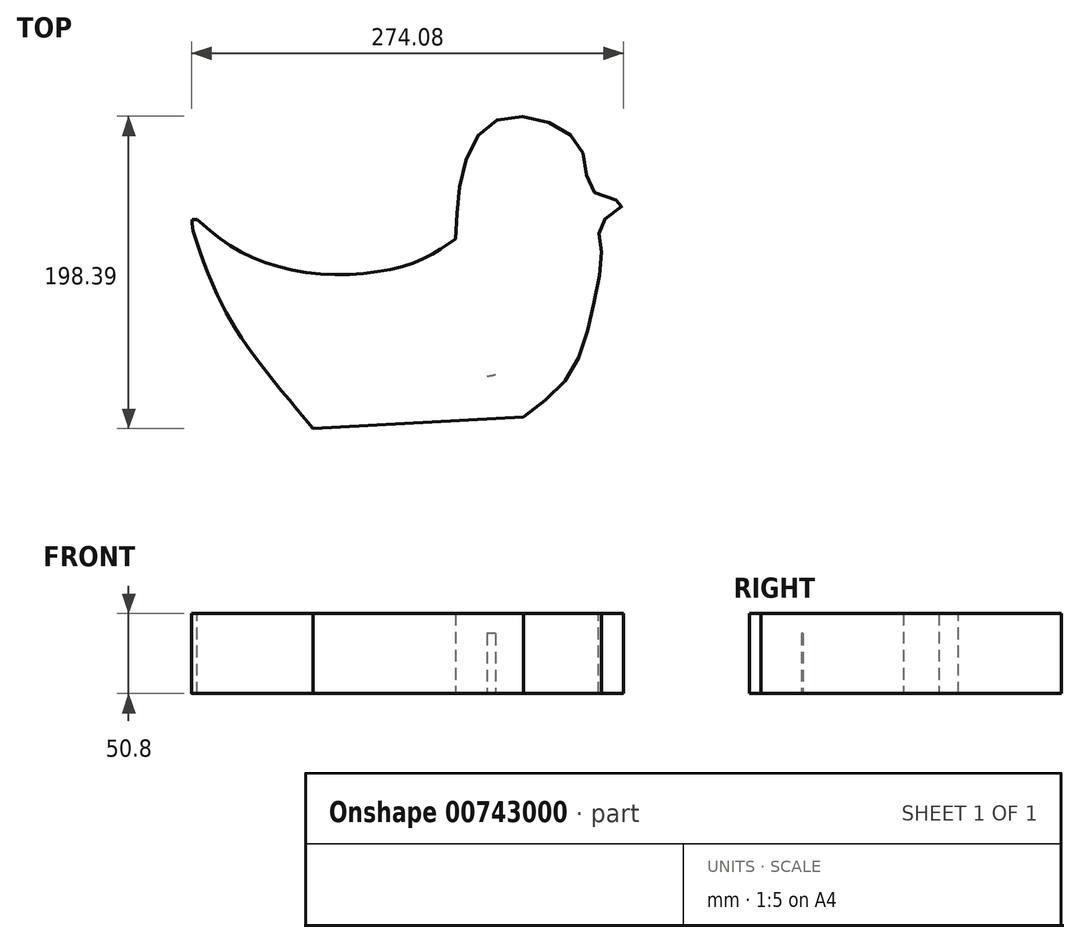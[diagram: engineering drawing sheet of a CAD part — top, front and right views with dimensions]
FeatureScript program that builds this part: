
annotation { "Feature Type Name" : "Feature", "Feature Type Description" : "" }
export const myFeature = defineFeature(function(context is Context, id is Id, definition is map)
    precondition{}
    {
        {
            var Q0;
            Q0=qCreatedBy(makeId("Top.planeOp"),FACE);
            var sketch = newSketch(context, id + "F0", { "sketchPlane" : qUnion([Q0])});
            skFitSpline(sketch, "E0", {"points": [v(27.43, 46.59) * mm, v(31.17, 85.8) * mm, v(49.84, 120.35) * mm, v(87.2, 120.35) * mm, v(108.7, 99.83) * mm, v(115.2, 76.47) * mm, v(133.88, 69) * mm, v(119.87, 56.86) * mm, v(119.87, 41.92) * mm, v(115.2, 6.44) * mm, v(101.2, -37.45) * mm, v(70.38, -66.4) * mm], "startDerivative": vector(11.43, 373.06) * mm, "endDerivative": vector(-329.68, -239.67) * mm});
            skFitSpline(sketch, "E1", {"points": [v(27.43, 46.59) * mm, v(-1.51, 30.71) * mm, v(-65, 25.11) * mm, v(-121.96, 46.59) * mm, v(-139.7, 59.66) * mm, v(-128.5, 21.38) * mm, v(-104.22, -22.5) * mm, v(-63.14, -73.86) * mm], "startDerivative": vector(-209.13, -145.94) * mm, "endDerivative": vector(263.47, -313.72) * mm});
            skLineSegment(sketch, "E2", {"start": v(-63.14, -73.86) * mm, "end": v(70.38, -66.4) * mm});
            skCircle(sketch, "E3", {"center": v(41.74, 2.68) * mm, "radius": 12.7 * mm});
            skSolve(sketch);
        }
        {
            var Q0;
            Q0=makeQuery(id+"F0.imprint","IMPRINT",FACE,{"disambiguationData":[TD([[makeQuery(id+"F0.imprint","IMPRINT",EDGE,{"derivedFrom":sQuery(id+"F0.wireOp",EDGE,"E0")}),-1.0]])]});
            var Q1;
            Q1=makeQuery(id+"F0.imprint","IMPRINT",FACE,{"disambiguationData":[TD([[makeQuery(id+"F0.imprint","IMPRINT",EDGE,{"derivedFrom":sQuery(id+"F0.wireOp",EDGE,"E3")}),1.0]])]});
            extrude(context, id + "F1", {"entities" : qUnion([Q0, Q1]), "depth" : 50.8 * mm, "offsetDistance" : 25.4 * mm});
        }
        {
            var Q0;
            Q0=makeQuery(id+"F1.opExtrude","CAP_FACE",FACE,{"disambiguationData":[OSD([sQuery(id+"F0.wireOp",EDGE,"E0"),sQuery(id+"F0.wireOp",EDGE,"E1"),sQuery(id+"F0.wireOp",EDGE,"E2")])],"isStart":true});
            var sketch = newSketch(context, id + "F2", { "sketchPlane" : qUnion([Q0])});
            skFitSpline(sketch, "E4", {"points": [v(27.43, -46.59) * mm, v(39.45, -47.43) * mm, v(51.84, -46.33) * mm, v(60.82, -43.18) * mm, v(73.52, -34.07) * mm, v(81, -23.77) * mm, v(85.37, -11.03) * mm, v(85.6, 3.2) * mm, v(80.9, 17.59) * mm, v(70.26, 30.74) * mm, v(52.63, 39.76) * mm, v(41, 40.84) * mm], "startDerivative": vector(141.59, -14.35) * mm, "endDerivative": vector(-205.7, 0.46) * mm});
            skFitSpline(sketch, "E5", {"points": [v(46.72, 40.82) * mm, v(-31.66, 44.18) * mm, v(-45.45, 40.82) * mm, v(-73.03, 4.17) * mm, v(-98.8, -33.67) * mm], "startDerivative": vector(-265.25, 13.6) * mm, "endDerivative": vector(-93.78, -135.63) * mm});
            skLineSegment(sketch, "E6", {"start": v(52.63, 39.76) * mm, "end": v(46.72, 40.82) * mm});
            skSolve(sketch);
        }
        {
            var Q0;
            Q0 = qSketchRegion(id + "F2", true);
            extrude(context, id + "F3", {"entities" : qUnion([Q0]), "operationType" : NewBodyOperationType.ADD, "oppositeDirection" : true, "depth" : 25.4 * mm, "offsetDistance" : 25.4 * mm});
        }
        {
            var Q0;
            {var subQ0=sQuery(id+"F2.wireOp",EDGE,"E4");Q0=makeQuery(id+"F2.imprint","IMPRINT",FACE,{"disambiguationData":[TD([[makeQuery(id+"F2.imprint","IMPRINT",EDGE,{"derivedFrom":subQ0}),1.0]])]});}
            extrude(context, id + "F4", {"entities" : qUnion([Q0]), "operationType" : NewBodyOperationType.REMOVE, "oppositeDirection" : true, "depth" : 38.1 * mm, "offsetDistance" : 25.4 * mm});
        }
        {
            var Q0;
            Q0=makeQuery(id+"F4.boolean.opBoolean","COPY",FACE,{"derivedFrom":makeQuery(id+"F4.opExtrude","CAP_FACE",FACE,{"disambiguationData":[OSD([sQuery(id+"F0.wireOp",EDGE,"E1"),sQuery(id+"F2.wireOp",EDGE,"E4"),sQuery(id+"F2.wireOp",EDGE,"E5"),sQuery(id+"F2.wireOp",EDGE,"E6")])],"isStart":false})});
            var sketch = newSketch(context, id + "F5", { "sketchPlane" : qUnion([Q0])});
            skCircle(sketch, "E7", {"center": v(41.3, -3.91) * mm, "radius": 12.7 * mm});
            skSolve(sketch);
        }
        {
            var Q0;
            Q0=makeQuery(id+"F5.imprint","IMPRINT",FACE,{"disambiguationData":[TD([[makeQuery(id+"F5.imprint","IMPRINT",EDGE,{"derivedFrom":sQuery(id+"F5.wireOp",EDGE,"E7")}),1.0]])]});
            extrude(context, id + "F6", {"entities" : qUnion([Q0]), "operationType" : NewBodyOperationType.ADD, "depth" : 38.1 * mm, "offsetDistance" : 25.4 * mm});
        }
        {
            var Q0;
            Q0=makeQuery(id+"F1.opExtrude","CAP_FACE",FACE,{"disambiguationData":[OSD([sQuery(id+"F0.wireOp",EDGE,"E0"),sQuery(id+"F0.wireOp",EDGE,"E1"),sQuery(id+"F0.wireOp",EDGE,"E2")])],"isStart":false});
            var sketch = newSketch(context, id + "F7", { "sketchPlane" : qUnion([Q0])});
            skLineSegment(sketch, "E8", {"start": v(-140.02, 59.1) * mm, "end": v(-136.85, 58.94) * mm});
            skSolve(sketch);
        }
        {
            var Q0;
            {var subQ0=sQuery(id+"F7.wireOp",EDGE,"E8");Q0=makeQuery(id+"F7.imprint","IMPRINT",FACE,{"disambiguationData":[TD([[makeQuery(id+"F7.imprint","IMPRINT",EDGE,{"derivedFrom":subQ0}),1.0]])]});}
            extrude(context, id + "F8", {"entities" : qUnion([Q0]), "operationType" : NewBodyOperationType.REMOVE, "oppositeDirection" : true, "depth" : 57.15 * mm, "offsetDistance" : 25.4 * mm});
        }
    });
